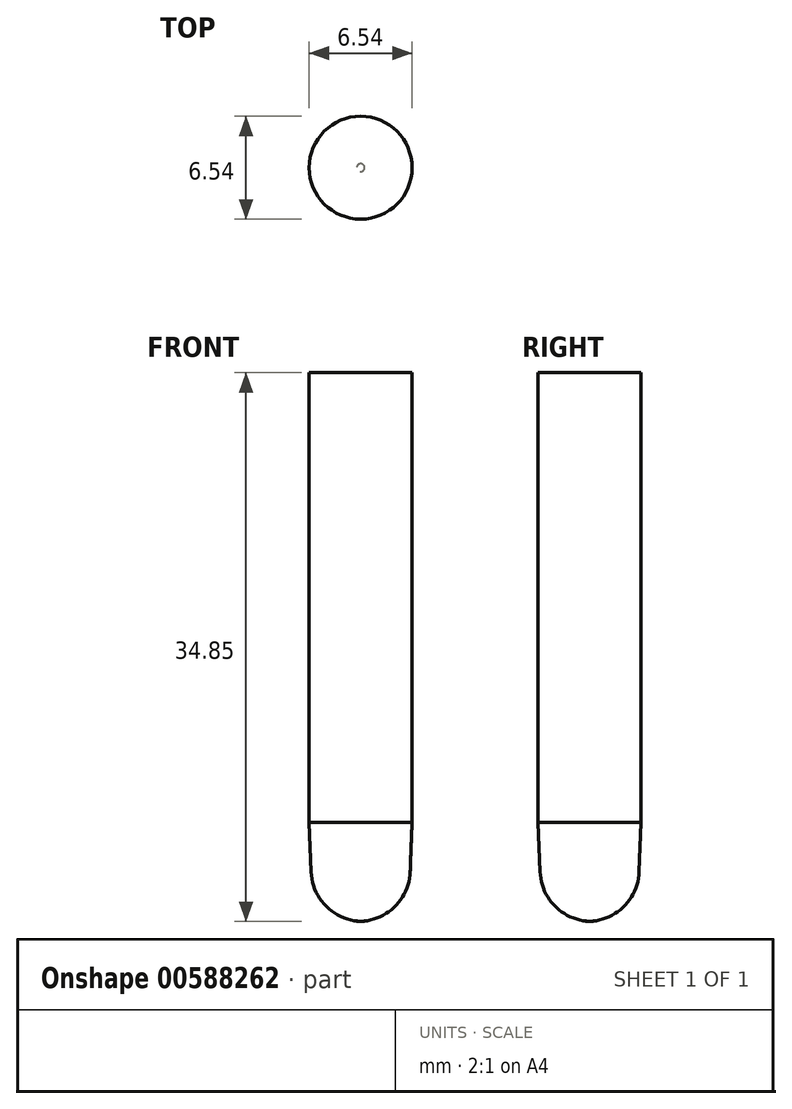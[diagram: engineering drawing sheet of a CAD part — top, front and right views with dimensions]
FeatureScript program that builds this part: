
annotation { "Feature Type Name" : "Feature", "Feature Type Description" : "" }
export const myFeature = defineFeature(function(context is Context, id is Id, definition is map)
    precondition{}
    {
        {
            var Q0;
            Q0=qCreatedBy(makeId("Front.planeOp"),FACE);
            var sketch = newSketch(context, id + "F0", { "sketchPlane" : qUnion([Q0])});
            skLineSegment(sketch, "E0.bottom", {"start": v(-60.67, 57.08) * mm, "end": v(-57.4, 57.08) * mm});
            skLineSegment(sketch, "E0.top", {"start": v(-60.67, 28.52) * mm, "end": v(-57.4, 28.52) * mm});
            skLineSegment(sketch, "E0.left", {"start": v(-60.67, 57.08) * mm, "end": v(-60.67, 28.52) * mm});
            skLineSegment(sketch, "E0.right", {"start": v(-57.4, 57.08) * mm, "end": v(-57.4, 28.52) * mm});
            skLineSegment(sketch, "E1", {"start": v(-57.4, 28.52) * mm, "end": v(-57.4, 25.38) * mm});
            skLineSegment(sketch, "E2", {"start": v(-60.55, 25.38) * mm, "end": v(-60.67, 28.52) * mm});
            skLineSegment(sketch, "E3", {"start": v(-57.4, 28.52) * mm, "end": v(-57.4, 22.23) * mm});
            skArc(sketch, "E4", {"start": v(-60.55, 25.38) * mm, "mid": v(-59.6, 23.19) * mm, "end": v(-57.4, 22.23) * mm});
            skSolve(sketch);
        }
        {
            var Q0;
            {var subQ0=sQuery(id+"F0.wireOp",EDGE,"E0.top");Q0=makeQuery(id+"F0.imprint","IMPRINT",FACE,{"disambiguationData":[TD([[makeQuery(id+"F0.imprint","IMPRINT",EDGE,{"derivedFrom":subQ0}),-1.0]])]});}
            var Q1;
            Q1=makeQuery(id+"F0.imprint","IMPRINT",FACE,{"disambiguationData":[TD([[makeQuery(id+"F0.imprint","IMPRINT",EDGE,{"derivedFrom":sQuery(id+"F0.wireOp",EDGE,"E0.bottom")}),-1.0]])]});
            var Q2;
            Q2=sQuery(id+"F0.wireOp",EDGE,"E0.right");
            revolve(context, id + "F1", {"entities" : qUnion([Q0, Q1]), "axis" : qUnion([Q2]), "revolveType" : RevolveType.FULL});
        }
    });
